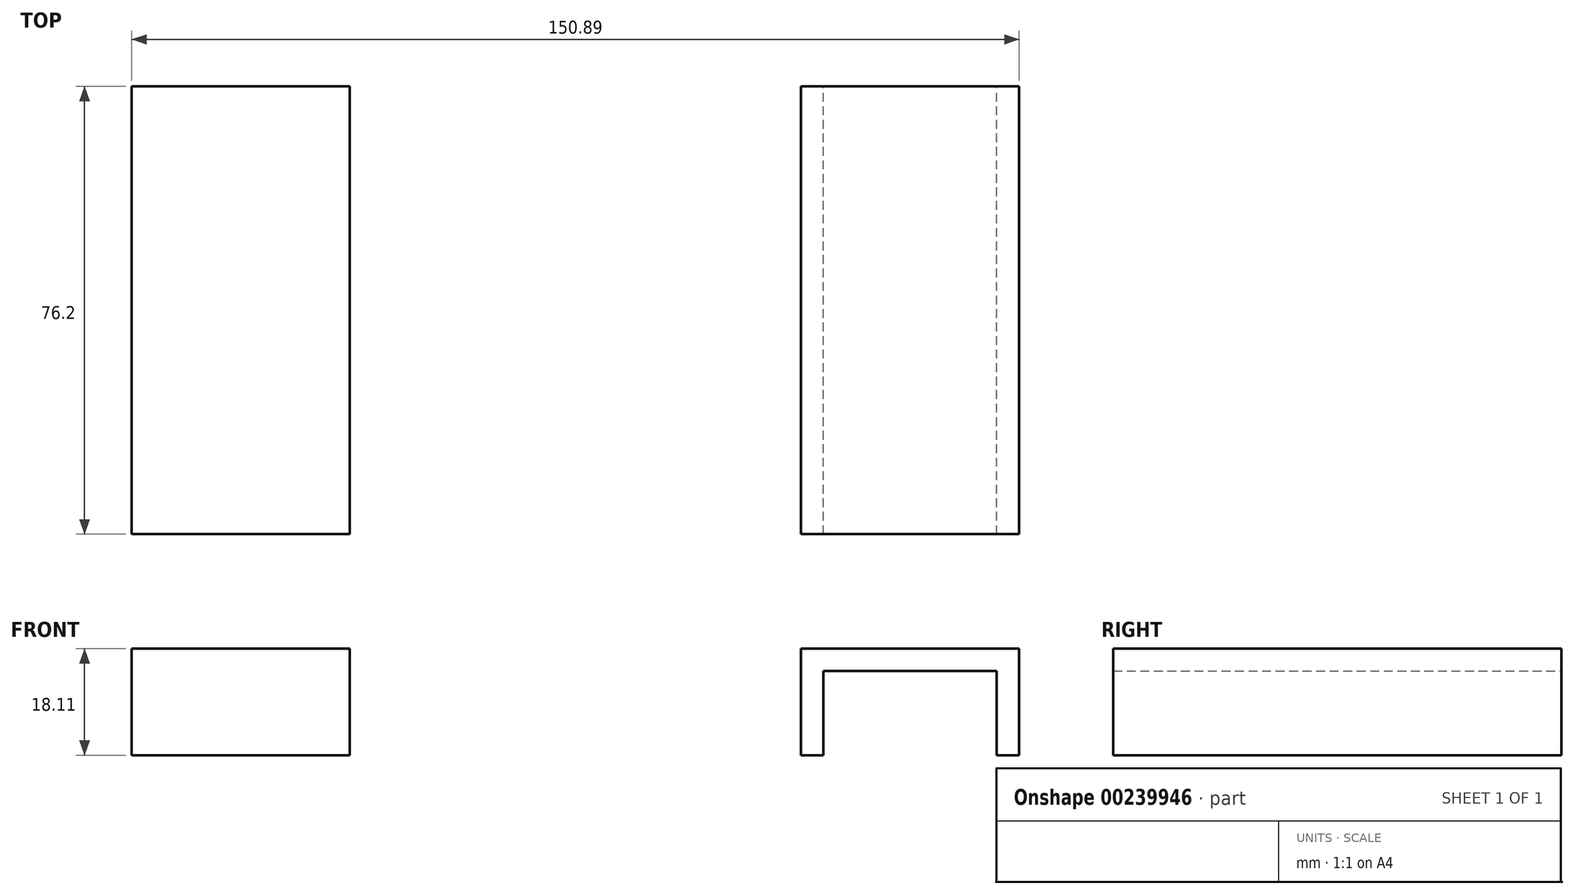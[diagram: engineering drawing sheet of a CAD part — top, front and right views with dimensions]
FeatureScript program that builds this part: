
annotation { "Feature Type Name" : "Feature", "Feature Type Description" : "" }
export const myFeature = defineFeature(function(context is Context, id is Id, definition is map)
    precondition{}
    {
        {
            var Q0;
            Q0=qCreatedBy(makeId("Front.planeOp"),FACE);
            var sketch = newSketch(context, id + "F0", { "sketchPlane" : qUnion([Q0])});
            skLineSegment(sketch, "E0.bottom", {"start": v(-39.08, 0) * mm, "end": v(-76.16, 0) * mm});
            skLineSegment(sketch, "E0.top", {"start": v(-39.08, 18.11) * mm, "end": v(-76.16, 18.11) * mm});
            skLineSegment(sketch, "E0.left", {"start": v(-39.08, 0) * mm, "end": v(-39.08, 18.11) * mm});
            skLineSegment(sketch, "E0.right", {"start": v(-76.16, 0) * mm, "end": v(-76.16, 18.11) * mm});
            skLineSegment(sketch, "E1.bottom", {"start": v(37.65, 0) * mm, "end": v(74.73, 0) * mm});
            skLineSegment(sketch, "E1.top", {"start": v(37.65, 18.11) * mm, "end": v(74.73, 18.11) * mm});
            skLineSegment(sketch, "E1.left", {"start": v(37.65, 0) * mm, "end": v(37.65, 18.11) * mm});
            skLineSegment(sketch, "E1.right", {"start": v(74.73, 0) * mm, "end": v(74.73, 18.11) * mm});
            skSolve(sketch);
        }
        {
            var Q0;
            Q0=makeQuery(id+"F0.imprint","IMPRINT",FACE,{"disambiguationData":[TD([[makeQuery(id+"F0.imprint","IMPRINT",EDGE,{"derivedFrom":sQuery(id+"F0.wireOp",EDGE,"E1.bottom")}),1.0]])]});
            var Q1;
            Q1=makeQuery(id+"F0.imprint","IMPRINT",FACE,{"disambiguationData":[TD([[makeQuery(id+"F0.imprint","IMPRINT",EDGE,{"derivedFrom":sQuery(id+"F0.wireOp",EDGE,"E0.bottom")}),-1.0]])]});
            extrude(context, id + "F1", {"entities" : qUnion([Q0, Q1]), "depth" : 76.2 * mm});
        }
        {
            var Q0;
            Q0=makeQuery(id+"F0.imprint","IMPRINT",FACE,{"disambiguationData":[TD([[makeQuery(id+"F0.imprint","IMPRINT",EDGE,{"derivedFrom":sQuery(id+"F0.wireOp",EDGE,"E1.bottom")}),1.0]])]});
            var Q1;
            Q1=makeQuery(id+"F0.imprint","IMPRINT",FACE,{"disambiguationData":[TD([[makeQuery(id+"F0.imprint","IMPRINT",EDGE,{"derivedFrom":sQuery(id+"F0.wireOp",EDGE,"E0.bottom")}),-1.0]])]});
            extrude(context, id + "F2", {"entities" : qUnion([Q0, Q1]), "oppositeDirection" : true, "depth" : 76.2 * mm});
        }
        {
            var Q0;
            Q0=makeQuery(id+"F2.opExtrude","CAP_FACE",FACE,{"disambiguationData":[OSD([sQuery(id+"F0.wireOp",EDGE,"E1.bottom"),sQuery(id+"F0.wireOp",EDGE,"E1.top"),sQuery(id+"F0.wireOp",EDGE,"E1.left"),sQuery(id+"F0.wireOp",EDGE,"E1.right")])],"isStart":false});
            var sketch = newSketch(context, id + "F3", { "sketchPlane" : qUnion([Q0])});
            skLineSegment(sketch, "E2.bottom", {"start": v(-41.46, 0) * mm, "end": v(-70.92, 0) * mm});
            skLineSegment(sketch, "E2.top", {"start": v(-41.46, 14.3) * mm, "end": v(-70.92, 14.3) * mm});
            skLineSegment(sketch, "E2.left", {"start": v(-41.46, 0) * mm, "end": v(-41.46, 14.3) * mm});
            skLineSegment(sketch, "E2.right", {"start": v(-70.92, 0) * mm, "end": v(-70.92, 14.3) * mm});
            skSolve(sketch);
        }
        {
            var Q0;
            Q0 = qSketchRegion(id + "F3", true);
            var Q1;
            Q1 = qSketchRegion(id + "F0", true);
            extrude(context, id + "F4", {"entities" : qUnion([Q0, Q1]), "operationType" : NewBodyOperationType.REMOVE, "oppositeDirection" : true, "depth" : 152.4 * mm});
        }
    });
